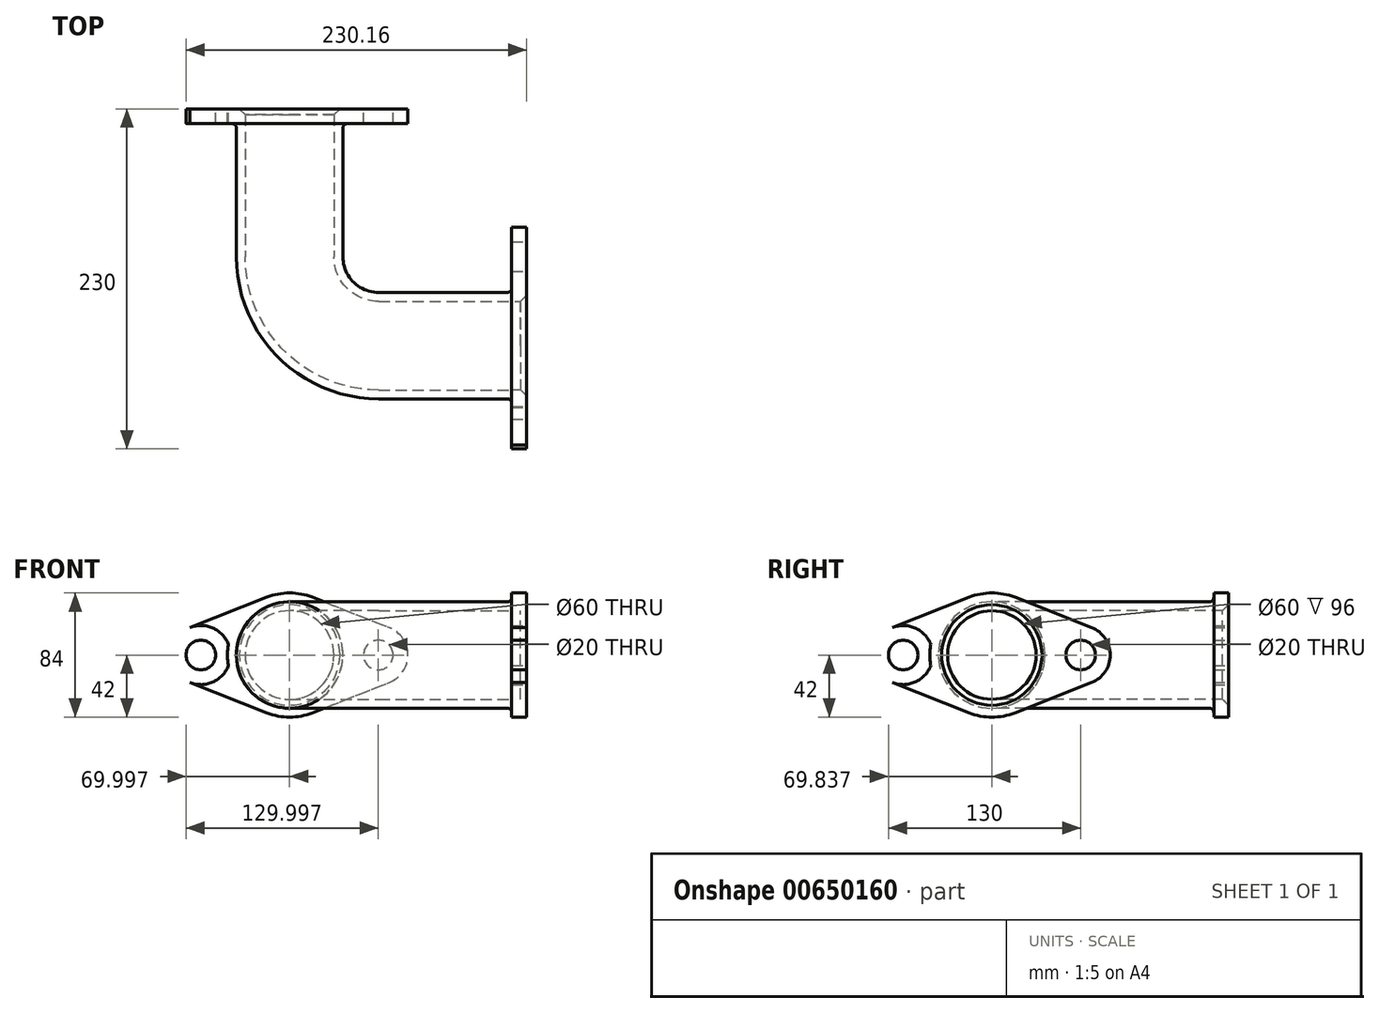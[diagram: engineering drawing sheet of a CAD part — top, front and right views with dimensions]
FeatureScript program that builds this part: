
annotation { "Feature Type Name" : "Feature", "Feature Type Description" : "" }
export const myFeature = defineFeature(function(context is Context, id is Id, definition is map)
    precondition{}
    {
        {
            var Q0;
            Q0=qCreatedBy(makeId("Top.planeOp"),FACE);
            var sketch = newSketch(context, id + "F0", { "sketchPlane" : qUnion([Q0])});
            skLineSegment(sketch, "E0", {"start": v(0, 0) * mm, "end": v(-100, 0) * mm});
            skLineSegment(sketch, "E1", {"start": v(-160, 60) * mm, "end": v(-160, 160) * mm});
            skPoint(sketch, "E2.visualSharp", {"position": v(-160, 0) * mm});
            skArc(sketch, "E2.filletArc", {"start": v(-160, 60) * mm, "mid": v(-142.43, 17.57) * mm, "end": v(-100, 0) * mm});
            skSolve(sketch);
        }
        {
            var Q0;
            Q0=qCreatedBy(makeId("Right.planeOp"),FACE);
            var sketch = newSketch(context, id + "F1", { "sketchPlane" : qUnion([Q0])});
            skCircle(sketch, "E3", {"center": v(0, 0) * mm, "radius": 30 * mm});
            skCircle(sketch, "E4", {"center": v(0, 0) * mm, "radius": 36 * mm});
            skCircle(sketch, "E5", {"center": v(60, 0) * mm, "radius": 10 * mm});
            skCircle(sketch, "E6", {"center": v(60, 0) * mm, "radius": 20 * mm});
            skLineSegment(sketch, "E7", {"start": v(-29.57, 56.8) * mm, "end": v(102.36, 4.8) * mm});
            skCircle(sketch, "E8", {"center": v(0, 0) * mm, "radius": 42 * mm});
            skLineSegment(sketch, "E9.MirrorCS", {"start": v(-29.57, -56.8) * mm, "end": v(102.36, -4.8) * mm});
            skLineSegment(sketch, "E10.MirrorCS", {"start": v(29.57, 56.8) * mm, "end": v(-102.36, 4.8) * mm});
            skCircle(sketch, "E11.MirrorC", {"center": v(-60, 0) * mm, "radius": 20 * mm});
            skCircle(sketch, "E12.MirrorC", {"center": v(-60, 0) * mm, "radius": 10 * mm});
            skLineSegment(sketch, "E13.MirrorCS", {"start": v(29.57, -56.8) * mm, "end": v(-102.36, -4.8) * mm});
            skSolve(sketch);
        }
        {
            var Q0;
            Q0=qCreatedBy(makeId("Front.planeOp"),FACE);
            cPlane(context, id + "F2", {"entities" : qUnion([Q0]), "cplaneType" : CPlaneType.OFFSET, "offset" : 160 * mm, "oppositeDirection" : true, "width" : 150 * mm, "height" : 150 * mm});
        }
        {
            var Q0;
            Q0=qCreatedBy(id+"F2.planeOp",FACE);
            var sketch = newSketch(context, id + "F3", { "sketchPlane" : qUnion([Q0])});
            skCircle(sketch, "E14", {"center": v(-160.16, 0) * mm, "radius": 30 * mm});
            skCircle(sketch, "E15", {"center": v(-160.16, 0) * mm, "radius": 36 * mm});
            skCircle(sketch, "E16", {"center": v(-100.16, 0) * mm, "radius": 10 * mm});
            skCircle(sketch, "E17", {"center": v(-100.16, 0) * mm, "radius": 20 * mm});
            skLineSegment(sketch, "E18", {"start": v(-189.74, 56.8) * mm, "end": v(-57.8, 4.8) * mm});
            skCircle(sketch, "E19", {"center": v(-160.16, 0) * mm, "radius": 42 * mm});
            skLineSegment(sketch, "E20.MirrorCS", {"start": v(-189.74, -56.8) * mm, "end": v(-57.8, -4.8) * mm});
            skLineSegment(sketch, "E21.MirrorCS", {"start": v(-130.59, 56.8) * mm, "end": v(-262.52, 4.8) * mm});
            skCircle(sketch, "E22.MirrorC", {"center": v(-220.16, 0) * mm, "radius": 20 * mm});
            skCircle(sketch, "E23.MirrorC", {"center": v(-220.16, 0) * mm, "radius": 10 * mm});
            skLineSegment(sketch, "E24.MirrorCS", {"start": v(-130.59, -56.8) * mm, "end": v(-262.52, -4.8) * mm});
            skSolve(sketch);
        }
        {
            var Q0;
            Q0=makeQuery(id+"F3.imprint","IMPRINT",FACE,{"disambiguationData":[TD([[makeQuery(id+"F3.imprint","IMPRINT",EDGE,{"derivedFrom":sQuery(id+"F3.wireOp",EDGE,"E14")}),-1.0]])]});
            var Q1;
            Q1=sQuery(id+"F0.wireOp",EDGE,"E1");
            var Q2;
            Q2=sQuery(id+"F0.wireOp",EDGE,"E2.filletArc");
            var Q3;
            Q3=sQuery(id+"F0.wireOp",EDGE,"E0");
            sweep(context, id + "F4", {"profiles" : qUnion([Q0]), "path" : qUnion([Q1, Q2, Q3])});
        }
        {
            var Q0;
            Q0=makeQuery(id+"F3.imprint","IMPRINT",FACE,{"disambiguationData":[TD([[makeQuery(id+"F3.imprint","IMPRINT",EDGE,{"derivedFrom":sQuery(id+"F3.wireOp",EDGE,"E23.MirrorC")}),1.0]])]});
            var Q1;
            {var subQ0=sQuery(id+"F3.wireOp",EDGE,"E21.MirrorCS");var subQ1=sQuery(id+"F3.wireOp",EDGE,"E19");var subQ2=makeQuery(id+"F3.imprint","INTERSECT",VERTEX,{"derivedFrom":[subQ1,subQ0]});Q1=makeQuery(id+"F3.imprint","IMPRINT",FACE,{"disambiguationData":[TD([[makeQuery(id+"F3.imprint","IMPRINT",EDGE,{"disambiguationData":[TD([[subQ2,-1.0]])],"derivedFrom":subQ1}),-1.0]])]});}
            var Q2;
            Q2=makeQuery(id+"F3.imprint","IMPRINT",FACE,{"disambiguationData":[TD([[makeQuery(id+"F3.imprint","IMPRINT",EDGE,{"derivedFrom":sQuery(id+"F3.wireOp",EDGE,"E15")}),-1.0]])]});
            var Q3;
            {var subQ0=sQuery(id+"F3.wireOp",EDGE,"E22.MirrorC");var subQ1=sQuery(id+"F3.wireOp",EDGE,"E19");var subQ2=makeQuery(id+"F3.imprint","INTERSECT",VERTEX,{"disambiguationData":[OD(0.0)],"derivedFrom":[subQ1,subQ0]});Q3=makeQuery(id+"F3.imprint","IMPRINT",FACE,{"disambiguationData":[TD([[makeQuery(id+"F3.imprint","IMPRINT",EDGE,{"disambiguationData":[TD([[subQ2,-1.0]])],"derivedFrom":subQ1}),1.0]])]});}
            var Q4;
            {var subQ0=sQuery(id+"F3.wireOp",EDGE,"E24.MirrorCS");var subQ1=sQuery(id+"F3.wireOp",EDGE,"E19");var subQ2=makeQuery(id+"F3.imprint","INTERSECT",VERTEX,{"derivedFrom":[subQ1,subQ0]});Q4=makeQuery(id+"F3.imprint","IMPRINT",FACE,{"disambiguationData":[TD([[makeQuery(id+"F3.imprint","IMPRINT",EDGE,{"disambiguationData":[TD([[subQ2,1.0]])],"derivedFrom":subQ1}),-1.0]])]});}
            var Q5;
            {var subQ0=sQuery(id+"F3.wireOp",EDGE,"E18");var subQ1=sQuery(id+"F3.wireOp",EDGE,"E17");var subQ2=makeQuery(id+"F3.imprint","INTERSECT",VERTEX,{"derivedFrom":[subQ1,subQ0]});Q5=makeQuery(id+"F3.imprint","IMPRINT",FACE,{"disambiguationData":[TD([[makeQuery(id+"F3.imprint","IMPRINT",EDGE,{"disambiguationData":[TD([[subQ2,-1.0]])],"derivedFrom":subQ1}),-1.0]])]});}
            var Q6;
            Q6=makeQuery(id+"F3.imprint","IMPRINT",FACE,{"disambiguationData":[TD([[makeQuery(id+"F3.imprint","IMPRINT",EDGE,{"derivedFrom":sQuery(id+"F3.wireOp",EDGE,"E16")}),-1.0]])]});
            var Q7;
            {var subQ0=sQuery(id+"F3.wireOp",EDGE,"E19");var subQ1=sQuery(id+"F3.wireOp",EDGE,"E17");var subQ2=makeQuery(id+"F3.imprint","INTERSECT",VERTEX,{"disambiguationData":[OD(0.0)],"derivedFrom":[subQ1,subQ0]});Q7=makeQuery(id+"F3.imprint","IMPRINT",FACE,{"disambiguationData":[TD([[makeQuery(id+"F3.imprint","IMPRINT",EDGE,{"disambiguationData":[TD([[subQ2,-1.0]])],"derivedFrom":subQ1}),1.0]])]});}
            var Q8;
            {var subQ0=sQuery(id+"F3.wireOp",EDGE,"E20.MirrorCS");var subQ1=sQuery(id+"F3.wireOp",EDGE,"E17");var subQ2=makeQuery(id+"F3.imprint","INTERSECT",VERTEX,{"derivedFrom":[subQ1,subQ0]});Q8=makeQuery(id+"F3.imprint","IMPRINT",FACE,{"disambiguationData":[TD([[makeQuery(id+"F3.imprint","IMPRINT",EDGE,{"disambiguationData":[TD([[subQ2,1.0]])],"derivedFrom":subQ1}),-1.0]])]});}
            var Q9;
            Q9=makeQuery(id+"F3.imprint","IMPRINT",FACE,{"disambiguationData":[TD([[makeQuery(id+"F3.imprint","IMPRINT",EDGE,{"derivedFrom":sQuery(id+"F3.wireOp",EDGE,"E14")}),-1.0]])]});
            extrude(context, id + "F5", {"entities" : qUnion([Q0, Q1, Q2, Q3, Q4, Q5, Q6, Q7, Q8, Q9]), "operationType" : NewBodyOperationType.ADD, "depth" : 10 * mm, "offsetDistance" : 25 * mm});
        }
        {
            var Q0;
            Q0=makeQuery(id+"F1.imprint","IMPRINT",FACE,{"disambiguationData":[TD([[makeQuery(id+"F1.imprint","IMPRINT",EDGE,{"derivedFrom":sQuery(id+"F1.wireOp",EDGE,"E4")}),-1.0]])]});
            var Q1;
            Q1=makeQuery(id+"F1.imprint","IMPRINT",FACE,{"disambiguationData":[TD([[makeQuery(id+"F1.imprint","IMPRINT",EDGE,{"derivedFrom":sQuery(id+"F1.wireOp",EDGE,"E3")}),-1.0]])]});
            var Q2;
            {var subQ0=sQuery(id+"F1.wireOp",EDGE,"E9.MirrorCS");var subQ1=sQuery(id+"F1.wireOp",EDGE,"E6");var subQ2=makeQuery(id+"F1.imprint","INTERSECT",VERTEX,{"derivedFrom":[subQ1,subQ0]});Q2=makeQuery(id+"F1.imprint","IMPRINT",FACE,{"disambiguationData":[TD([[makeQuery(id+"F1.imprint","IMPRINT",EDGE,{"disambiguationData":[TD([[subQ2,1.0]])],"derivedFrom":subQ1}),-1.0]])]});}
            var Q3;
            Q3=makeQuery(id+"F1.imprint","IMPRINT",FACE,{"disambiguationData":[TD([[makeQuery(id+"F1.imprint","IMPRINT",EDGE,{"derivedFrom":sQuery(id+"F1.wireOp",EDGE,"E5")}),-1.0]])]});
            var Q4;
            {var subQ0=sQuery(id+"F1.wireOp",EDGE,"E7");var subQ1=sQuery(id+"F1.wireOp",EDGE,"E6");var subQ2=makeQuery(id+"F1.imprint","INTERSECT",VERTEX,{"derivedFrom":[subQ1,subQ0]});Q4=makeQuery(id+"F1.imprint","IMPRINT",FACE,{"disambiguationData":[TD([[makeQuery(id+"F1.imprint","IMPRINT",EDGE,{"disambiguationData":[TD([[subQ2,-1.0]])],"derivedFrom":subQ1}),-1.0]])]});}
            var Q5;
            {var subQ0=sQuery(id+"F1.wireOp",EDGE,"E8");var subQ1=sQuery(id+"F1.wireOp",EDGE,"E6");var subQ2=makeQuery(id+"F1.imprint","INTERSECT",VERTEX,{"disambiguationData":[OD(0.0)],"derivedFrom":[subQ1,subQ0]});Q5=makeQuery(id+"F1.imprint","IMPRINT",FACE,{"disambiguationData":[TD([[makeQuery(id+"F1.imprint","IMPRINT",EDGE,{"disambiguationData":[TD([[subQ2,-1.0]])],"derivedFrom":subQ1}),1.0]])]});}
            var Q6;
            {var subQ0=sQuery(id+"F1.wireOp",EDGE,"E10.MirrorCS");var subQ1=sQuery(id+"F1.wireOp",EDGE,"E8");var subQ2=makeQuery(id+"F1.imprint","INTERSECT",VERTEX,{"derivedFrom":[subQ1,subQ0]});Q6=makeQuery(id+"F1.imprint","IMPRINT",FACE,{"disambiguationData":[TD([[makeQuery(id+"F1.imprint","IMPRINT",EDGE,{"disambiguationData":[TD([[subQ2,-1.0]])],"derivedFrom":subQ1}),-1.0]])]});}
            var Q7;
            Q7=makeQuery(id+"F1.imprint","IMPRINT",FACE,{"disambiguationData":[TD([[makeQuery(id+"F1.imprint","IMPRINT",EDGE,{"derivedFrom":sQuery(id+"F1.wireOp",EDGE,"E12.MirrorC")}),1.0]])]});
            var Q8;
            {var subQ0=sQuery(id+"F1.wireOp",EDGE,"E13.MirrorCS");var subQ1=sQuery(id+"F1.wireOp",EDGE,"E8");var subQ2=makeQuery(id+"F1.imprint","INTERSECT",VERTEX,{"derivedFrom":[subQ1,subQ0]});Q8=makeQuery(id+"F1.imprint","IMPRINT",FACE,{"disambiguationData":[TD([[makeQuery(id+"F1.imprint","IMPRINT",EDGE,{"disambiguationData":[TD([[subQ2,1.0]])],"derivedFrom":subQ1}),-1.0]])]});}
            var Q9;
            {var subQ0=sQuery(id+"F1.wireOp",EDGE,"E11.MirrorC");var subQ1=sQuery(id+"F1.wireOp",EDGE,"E8");var subQ2=makeQuery(id+"F1.imprint","INTERSECT",VERTEX,{"disambiguationData":[OD(0.0)],"derivedFrom":[subQ1,subQ0]});Q9=makeQuery(id+"F1.imprint","IMPRINT",FACE,{"disambiguationData":[TD([[makeQuery(id+"F1.imprint","IMPRINT",EDGE,{"disambiguationData":[TD([[subQ2,-1.0]])],"derivedFrom":subQ1}),1.0]])]});}
            extrude(context, id + "F6", {"entities" : qUnion([Q0, Q1, Q2, Q3, Q4, Q5, Q6, Q7, Q8, Q9]), "operationType" : NewBodyOperationType.ADD, "oppositeDirection" : true, "depth" : 10 * mm, "offsetDistance" : 25 * mm});
        }
        {
            var Q0;
            Q0=makeQuery(id+"F4.opSweep","CAP_EDGE",EDGE,{"disambiguationData":[OSD([sQuery(id+"F0.wireOp",VERTEX,"E0.start"),sQuery(id+"F3.wireOp",EDGE,"E14")])],"isStart":false});
            var Q1;
            Q1=makeQuery(id+"F4.opSweep","CAP_EDGE",EDGE,{"disambiguationData":[OSD([sQuery(id+"F0.wireOp",VERTEX,"E1.end"),sQuery(id+"F3.wireOp",EDGE,"E14")])],"isStart":true});
            chamfer(context, id + "F7", {"entities" : qUnion([Q0, Q1]), "width" : 4 * mm, "tangentPropagation" : true});
        }
        {
            var Q0;
            Q0=makeQuery(id+"F6.boolean.opBoolean","INTERSECT",EDGE,{"derivedFrom":[makeQuery(id+"F4.opSweep","SWEPT_FACE",FACE,{"disambiguationData":[OSD([sQuery(id+"F0.wireOp",EDGE,"E0"),sQuery(id+"F3.wireOp",EDGE,"E15")])]}),makeQuery(id+"F6.opExtrude","CAP_FACE",FACE,{"disambiguationData":[OSD([sQuery(id+"F1.wireOp",EDGE,"E3"),sQuery(id+"F1.wireOp",EDGE,"E5"),sQuery(id+"F1.wireOp",EDGE,"E6"),sQuery(id+"F1.wireOp",EDGE,"E7"),sQuery(id+"F1.wireOp",EDGE,"E8"),sQuery(id+"F1.wireOp",EDGE,"E9.MirrorCS"),sQuery(id+"F1.wireOp",EDGE,"E10.MirrorCS"),sQuery(id+"F1.wireOp",EDGE,"E11.MirrorC"),sQuery(id+"F1.wireOp",EDGE,"E12.MirrorC"),sQuery(id+"F1.wireOp",EDGE,"E13.MirrorCS")])],"isStart":false})]});
            var Q1;
            Q1=makeQuery(id+"F5.boolean.opBoolean","INTERSECT",EDGE,{"derivedFrom":[makeQuery(id+"F4.opSweep","SWEPT_FACE",FACE,{"disambiguationData":[OSD([sQuery(id+"F0.wireOp",EDGE,"E1"),sQuery(id+"F3.wireOp",EDGE,"E15")])]}),makeQuery(id+"F5.opExtrude","CAP_FACE",FACE,{"disambiguationData":[OSD([sQuery(id+"F3.wireOp",EDGE,"E14"),sQuery(id+"F3.wireOp",EDGE,"E16"),sQuery(id+"F3.wireOp",EDGE,"E17"),sQuery(id+"F3.wireOp",EDGE,"E18"),sQuery(id+"F3.wireOp",EDGE,"E19"),sQuery(id+"F3.wireOp",EDGE,"E20.MirrorCS"),sQuery(id+"F3.wireOp",EDGE,"E21.MirrorCS"),sQuery(id+"F3.wireOp",EDGE,"E22.MirrorC"),sQuery(id+"F3.wireOp",EDGE,"E23.MirrorC"),sQuery(id+"F3.wireOp",EDGE,"E24.MirrorCS")])],"isStart":false})]});
            fillet(context, id + "F8", {"entities" : qUnion([Q0, Q1]), "radius" : 3 * mm, "tangentPropagation" : true, "allowEdgeOverflow" : false});
        }
    });
